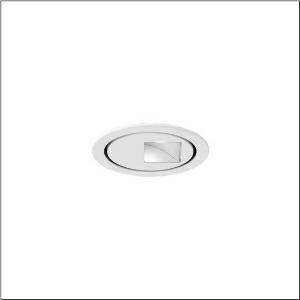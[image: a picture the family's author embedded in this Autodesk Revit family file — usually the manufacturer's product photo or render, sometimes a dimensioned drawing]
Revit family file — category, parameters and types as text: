
# Revit family: lunis_11_micro_round_51dj11b71wn21
name_source: partatom
category: Lighting Fixtures
units: mm (PartAtom-declared; Revit-internal decimal feet)

## family parameters
Cut with Voids When Loaded = No
Host = Face
Light Source = No
Part Type = Normal
Room Calculation Point = No
Round Connector Dimension = Use Diameter
Shared = No

## types (1)
- Lunis 11 micro round (1 x LED 4000K / CRI = 90 (unbekannt), 1210 lm, 4000K)
    Apparent Load = 20 VA
    CIE Flux Codes = 42 75 96 100 100
    Color Rendering = 90
    Color Temperature = 4000K
    Default Elevation = 1800 mm
    Description = Lunis 11 micro round, downlight, light control with wallwasher, of highly reflective aluminium, highly specular, light emission: direct distribution, LED rated luminous flux: 1.210lm, light colour: 940, with terminal, 3-pole, mains connection: 220..230V, AC, 50/60Hz, LED module, of aluminium, highly specular, white, diameter: 114mm, clamping range: 1..40mm, recessing ring, of plastic, traffic white (RAL 9016), protection rating (complete): IP20, insulation class (complete): insulation class II (safety insulation), certification: CE, permissible ambient temperature for indoor applications: 0..+35°C, packaging unit: 1 piece
    Height = 0 mm  [stored 0 ft]
    Lamp = 1 x LED 4000K / CRI >= 90 (unbekannt)
    Lamp Light Flux = 1210 lm
    Lamp count = 1
    Length = 114 mm
    Luminous efficacy = 61 lm/W
    Manufacturer = Siteco
    ModVariant = No
    Model = 51DJ11B71WN21
    Mounting Place = Ceiling
    Mounting Type = Recessed
    Number of Poles = 1
    OnlyDefault = Yes
    Power Factor = 1
    Product Name = Lunis 11 micro round
    Product group = downlight
    ProductGroupID = 401
    Protection Class = Protection class II
    Protection Degree = IP 20
    RLX_Detail_Level = 1
    RLX_Emergency_Light_Flux = 0 lm
    RLX_Emergency_Type = 0
    RLX_Emergency_Type_DB = No
    RlxData = <blob elided: 40517 chars, md5=f5a6dd58>
    Socket = socket
    Standby Power = 0 W
    System Light Flux = 1210 lm
    System Power = 20 W
    Type Comments = Product without accessories
    Type Image = l_1004773.jpg
    URL = http://relux.com
    VarID = ---
    Voltage = 0 V
    Weight = 0.00 kg
    Width = 114 mm

note: [stored X ft] marks values corroborated as IEEE doubles in the binary element streams (Revit-internal decimal feet)

## geometry (parser evidence)
native form markers: Blend x4, Sweep x9
no freeform markers — native parametric forms only
